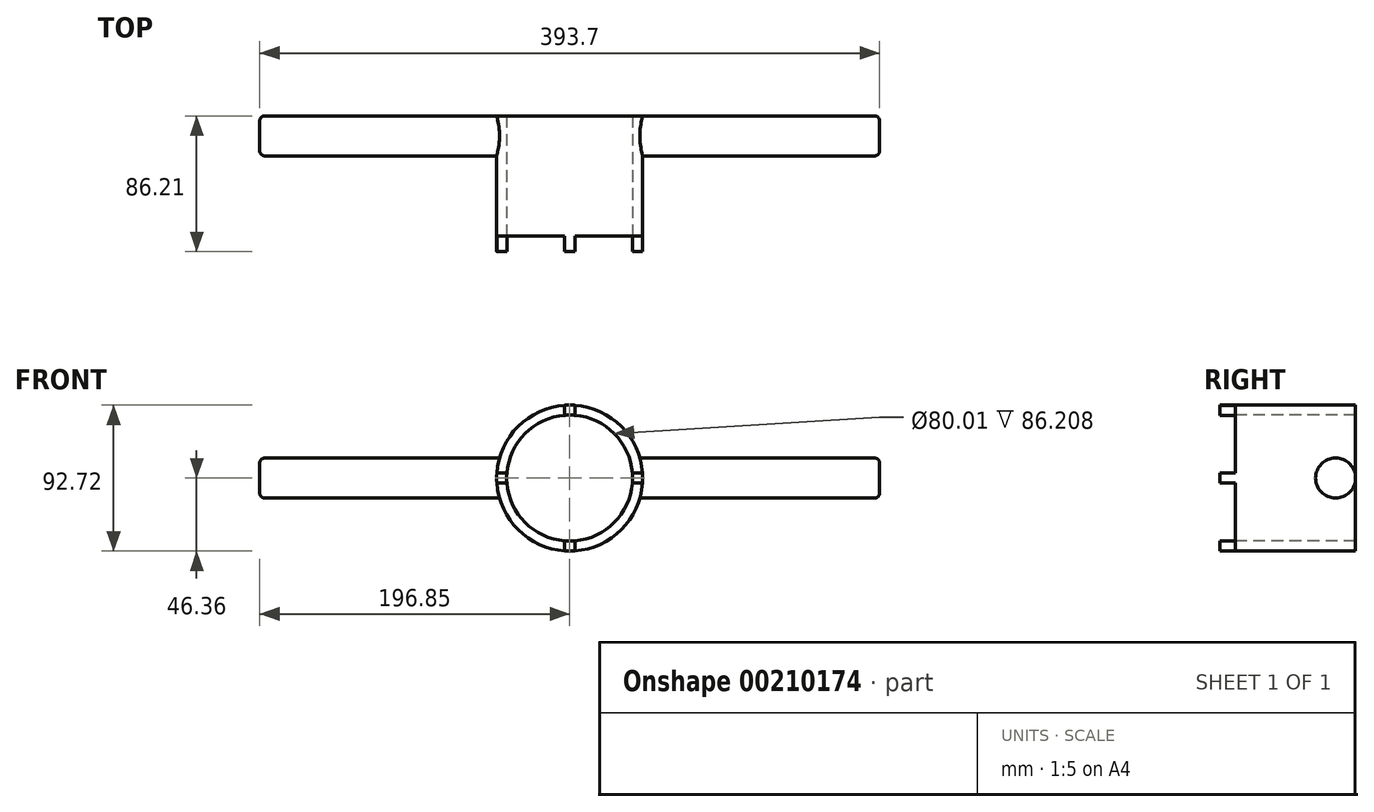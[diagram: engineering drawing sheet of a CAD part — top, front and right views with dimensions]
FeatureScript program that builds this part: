
annotation { "Feature Type Name" : "Feature", "Feature Type Description" : "" }
export const myFeature = defineFeature(function(context is Context, id is Id, definition is map)
    precondition{}
    {
        {
            var Q0;
            Q0=qCreatedBy(makeId("Front.planeOp"),FACE);
            var sketch = newSketch(context, id + "F0", { "sketchPlane" : qUnion([Q0])});
            skCircle(sketch, "E0", {"center": v(0, 0) * mm, "radius": 40 * mm});
            skCircle(sketch, "E1", {"center": v(0, 0) * mm, "radius": 46.35 * mm});
            skSolve(sketch);
        }
        {
            var Q0;
            Q0=makeQuery(id+"F0.imprint","IMPRINT",FACE,{"disambiguationData":[TD([[makeQuery(id+"F0.imprint","IMPRINT",EDGE,{"derivedFrom":sQuery(id+"F0.wireOp",EDGE,"E0")}),-1.0]])]});
            extrude(context, id + "F1", {"entities" : qUnion([Q0]), "oppositeDirection" : true, "depth" : 76.2 * mm});
        }
        {
            var Q0;
            Q0=makeQuery(id+"F1.opExtrude","CAP_FACE",FACE,{"disambiguationData":[OSD([sQuery(id+"F0.wireOp",EDGE,"E0"),sQuery(id+"F0.wireOp",EDGE,"E1")])],"isStart":true});
            var sketch = newSketch(context, id + "F2", { "sketchPlane" : qUnion([Q0])});
            skLineSegment(sketch, "E2.bottom", {"start": v(0, 48.23) * mm, "end": v(3.25, 48.23) * mm});
            skLineSegment(sketch, "E2.top", {"start": v(0, -47.48) * mm, "end": v(3.25, -47.48) * mm});
            skLineSegment(sketch, "E2.left", {"start": v(0, 48.23) * mm, "end": v(0, -47.48) * mm});
            skLineSegment(sketch, "E2.right", {"start": v(3.25, 48.23) * mm, "end": v(3.25, -47.48) * mm});
            skLineSegment(sketch, "E3.MirrorCS", {"start": v(0, 48.23) * mm, "end": v(-3.25, 48.23) * mm});
            skLineSegment(sketch, "E4.MirrorCS", {"start": v(-3.25, 48.23) * mm, "end": v(-3.25, -47.48) * mm});
            skLineSegment(sketch, "E5.MirrorCS", {"start": v(0, -47.48) * mm, "end": v(-3.25, -47.48) * mm});
            skSolve(sketch);
        }
        {
            var Q0;
            {var subQ0=sQuery(id+"F2.wireOp",EDGE,"E4.MirrorCS");var subQ1=makeQuery(id+"F1.opExtrude","CAP_EDGE",EDGE,{"disambiguationData":[OSD([sQuery(id+"F0.wireOp",EDGE,"E1")])],"isStart":true});var subQ2=makeQuery(id+"F2.imprint","INTERSECT",VERTEX,{"disambiguationData":[OD(0.0)],"derivedFrom":[subQ1,subQ0]});Q0=makeQuery(id+"F2.imprint","IMPRINT",FACE,{"disambiguationData":[TD([[makeQuery(id+"F2.imprint","IMPRINT",EDGE,{"disambiguationData":[TD([[subQ2,-1.0]])],"derivedFrom":subQ0}),-1.0]])]});}
            var sketch = newSketch(context, id + "F3", { "sketchPlane" : qUnion([Q0])});
            skLineSegment(sketch, "E6.bottom", {"start": v(0, 0) * mm, "end": v(50.37, 0) * mm});
            skLineSegment(sketch, "E6.top", {"start": v(0, 3.25) * mm, "end": v(50.37, 3.25) * mm});
            skLineSegment(sketch, "E6.left", {"start": v(0, 0) * mm, "end": v(0, 3.25) * mm});
            skLineSegment(sketch, "E6.right", {"start": v(50.37, 0) * mm, "end": v(50.37, 3.25) * mm});
            skLineSegment(sketch, "E7.MirrorCS", {"start": v(0, -3.25) * mm, "end": v(50.37, -3.25) * mm});
            skLineSegment(sketch, "E8.MirrorCS", {"start": v(50.37, 0) * mm, "end": v(50.37, -3.25) * mm});
            skLineSegment(sketch, "E9.MirrorCS", {"start": v(0, -3.25) * mm, "end": v(-50.37, -3.25) * mm});
            skLineSegment(sketch, "E10.MirrorCS", {"start": v(0, 3.25) * mm, "end": v(-50.37, 3.25) * mm});
            skLineSegment(sketch, "E11.MirrorCS", {"start": v(-50.37, 0) * mm, "end": v(-50.37, -3.25) * mm});
            skLineSegment(sketch, "E12.MirrorCS", {"start": v(-50.37, 0) * mm, "end": v(-50.37, 3.25) * mm});
            skSolve(sketch);
        }
        {
            var Q0;
            {var subQ0=sQuery(id+"F2.wireOp",EDGE,"E2.left");var subQ1=makeQuery(id+"F1.opExtrude","CAP_EDGE",EDGE,{"disambiguationData":[OSD([sQuery(id+"F0.wireOp",EDGE,"E1")])],"isStart":true});var subQ2=makeQuery(id+"F2.imprint","INTERSECT",VERTEX,{"disambiguationData":[OD(0.0)],"derivedFrom":[subQ1,subQ0]});Q0=makeQuery(id+"F2.imprint","IMPRINT",FACE,{"disambiguationData":[TD([[makeQuery(id+"F2.imprint","IMPRINT",EDGE,{"disambiguationData":[TD([[subQ2,-1.0]])],"derivedFrom":subQ0}),-1.0]])]});}
            var Q1;
            {var subQ0=sQuery(id+"F2.wireOp",EDGE,"E2.left");var subQ1=makeQuery(id+"F1.opExtrude","CAP_EDGE",EDGE,{"disambiguationData":[OSD([sQuery(id+"F0.wireOp",EDGE,"E1")])],"isStart":true});var subQ2=makeQuery(id+"F2.imprint","INTERSECT",VERTEX,{"disambiguationData":[OD(0.0)],"derivedFrom":[subQ1,subQ0]});Q1=makeQuery(id+"F2.imprint","IMPRINT",FACE,{"disambiguationData":[TD([[makeQuery(id+"F2.imprint","IMPRINT",EDGE,{"disambiguationData":[TD([[subQ2,-1.0]])],"derivedFrom":subQ0}),1.0]])]});}
            var Q2;
            {var subQ0=sQuery(id+"F2.wireOp",EDGE,"E2.left");var subQ1=makeQuery(id+"F1.opExtrude","CAP_EDGE",EDGE,{"disambiguationData":[OSD([sQuery(id+"F0.wireOp",EDGE,"E0")])],"isStart":true});var subQ2=makeQuery(id+"F2.imprint","INTERSECT",VERTEX,{"disambiguationData":[OD(1.0)],"derivedFrom":[subQ1,subQ0]});Q2=makeQuery(id+"F2.imprint","IMPRINT",FACE,{"disambiguationData":[TD([[makeQuery(id+"F2.imprint","IMPRINT",EDGE,{"disambiguationData":[TD([[subQ2,-1.0]])],"derivedFrom":subQ0}),1.0]])]});}
            var Q3;
            {var subQ0=sQuery(id+"F2.wireOp",EDGE,"E2.left");var subQ1=makeQuery(id+"F1.opExtrude","CAP_EDGE",EDGE,{"disambiguationData":[OSD([sQuery(id+"F0.wireOp",EDGE,"E0")])],"isStart":true});var subQ2=makeQuery(id+"F2.imprint","INTERSECT",VERTEX,{"disambiguationData":[OD(1.0)],"derivedFrom":[subQ1,subQ0]});Q3=makeQuery(id+"F2.imprint","IMPRINT",FACE,{"disambiguationData":[TD([[makeQuery(id+"F2.imprint","IMPRINT",EDGE,{"disambiguationData":[TD([[subQ2,-1.0]])],"derivedFrom":subQ0}),-1.0]])]});}
            var Q4;
            {var subQ0=sQuery(id+"F3.wireOp",EDGE,"E9.MirrorCS");var subQ1=sQuery(id+"F2.wireOp",EDGE,"E4.MirrorCS");var subQ2=makeQuery(id+"F1.opExtrude","CAP_EDGE",EDGE,{"disambiguationData":[OSD([sQuery(id+"F0.wireOp",EDGE,"E0")])],"isStart":true});var subQ3=makeQuery(id+"F2.imprint","IMPRINT",EDGE,{"disambiguationData":[TD([[makeQuery(id+"F2.imprint","INTERSECT",VERTEX,{"disambiguationData":[OD(0.0)],"derivedFrom":[subQ2,subQ1]}),-1.0]])],"derivedFrom":subQ2});var subQ4=makeQuery(id+"F3.imprint","INTERSECT",VERTEX,{"derivedFrom":[subQ3,subQ0]});Q4=makeQuery(id+"F3.imprint","IMPRINT",FACE,{"disambiguationData":[TD([[makeQuery(id+"F3.imprint","IMPRINT",EDGE,{"disambiguationData":[TD([[subQ4,-1.0]])],"derivedFrom":subQ0}),-1.0]])]});}
            extrude(context, id + "F4", {"entities" : qUnion([Q0, Q1, Q2, Q3, Q4]), "operationType" : NewBodyOperationType.ADD, "depth" : 10 * mm});
        }
        {
            var Q0;
            {var subQ0=sQuery(id+"F2.wireOp",EDGE,"E2.right");var subQ1=sQuery(id+"F0.wireOp",EDGE,"E1");var subQ2=makeQuery(id+"F1.opExtrude","CAP_EDGE",EDGE,{"disambiguationData":[OSD([subQ1])],"isStart":true});var subQ4=sQuery(id+"F0.wireOp",EDGE,"E0");var subQ16=makeQuery(id+"F2.imprint","INTERSECT",VERTEX,{"disambiguationData":[OD(0.0)],"derivedFrom":[subQ2,subQ0]});Q0=makeQuery(id+"F4.boolean.opBoolean","SPLIT",FACE,{"disambiguationData":[TD([makeQuery(id+"F4.opExtrude","SWEPT_FACE",FACE,{"disambiguationData":[OSD([subQ0]),TDD([makeQuery(id+"F2.imprint","IMPRINT",EDGE,{"disambiguationData":[TD([[subQ16,-1.0]])],"derivedFrom":subQ0})])]})])],"derivedFrom":makeQuery(id+"F1.opExtrude","CAP_FACE",FACE,{"disambiguationData":[OSD([subQ4,subQ1])],"isStart":true})});}
            var sketch = newSketch(context, id + "F5", { "sketchPlane" : qUnion([Q0])});
            skLineSegment(sketch, "E13.bottom", {"start": v(0, 0) * mm, "end": v(46.56, 0) * mm});
            skLineSegment(sketch, "E13.top", {"start": v(0, 3.25) * mm, "end": v(46.56, 3.25) * mm});
            skLineSegment(sketch, "E13.left", {"start": v(0, 0) * mm, "end": v(0, 3.25) * mm});
            skLineSegment(sketch, "E13.right", {"start": v(46.56, 0) * mm, "end": v(46.56, 3.25) * mm});
            skLineSegment(sketch, "E14.MirrorCS", {"start": v(0, -3.25) * mm, "end": v(46.56, -3.25) * mm});
            skLineSegment(sketch, "E15.MirrorCS", {"start": v(46.56, 0) * mm, "end": v(46.56, -3.25) * mm});
            skSolve(sketch);
        }
        {
            var Q0;
            {var subQ0=sQuery(id+"F5.wireOp",EDGE,"E13.bottom");var subQ1=sQuery(id+"F2.wireOp",EDGE,"E2.right");var subQ2=sQuery(id+"F0.wireOp",EDGE,"E1");var subQ3=makeQuery(id+"F1.opExtrude","CAP_EDGE",EDGE,{"disambiguationData":[OSD([subQ2])],"isStart":true});var subQ13=makeQuery(id+"F2.imprint","INTERSECT",VERTEX,{"disambiguationData":[OD(0.0)],"derivedFrom":[subQ3,subQ1]});var subQ15=makeQuery(id+"F4.opExtrude","SWEPT_FACE",FACE,{"disambiguationData":[OSD([subQ1]),TDD([makeQuery(id+"F2.imprint","IMPRINT",EDGE,{"disambiguationData":[TD([[subQ13,-1.0]])],"derivedFrom":subQ1})])]});var subQ29=makeQuery(id+"F4.boolean.opBoolean","SPLIT",EDGE,{"disambiguationData":[TD([subQ15])],"derivedFrom":subQ3});var subQ30=makeQuery(id+"F5.imprint","INTERSECT",VERTEX,{"derivedFrom":[subQ29,subQ0]});Q0=makeQuery(id+"F5.imprint","IMPRINT",FACE,{"disambiguationData":[TD([[makeQuery(id+"F5.imprint","IMPRINT",EDGE,{"disambiguationData":[TD([[subQ30,1.0]])],"derivedFrom":subQ0}),1.0]])]});}
            var Q1;
            {var subQ0=sQuery(id+"F5.wireOp",EDGE,"E13.bottom");var subQ1=sQuery(id+"F2.wireOp",EDGE,"E2.right");var subQ2=sQuery(id+"F0.wireOp",EDGE,"E1");var subQ3=makeQuery(id+"F1.opExtrude","CAP_EDGE",EDGE,{"disambiguationData":[OSD([subQ2])],"isStart":true});var subQ13=makeQuery(id+"F2.imprint","INTERSECT",VERTEX,{"disambiguationData":[OD(0.0)],"derivedFrom":[subQ3,subQ1]});var subQ15=makeQuery(id+"F4.opExtrude","SWEPT_FACE",FACE,{"disambiguationData":[OSD([subQ1]),TDD([makeQuery(id+"F2.imprint","IMPRINT",EDGE,{"disambiguationData":[TD([[subQ13,-1.0]])],"derivedFrom":subQ1})])]});var subQ29=makeQuery(id+"F4.boolean.opBoolean","SPLIT",EDGE,{"disambiguationData":[TD([subQ15])],"derivedFrom":subQ3});var subQ30=makeQuery(id+"F5.imprint","INTERSECT",VERTEX,{"derivedFrom":[subQ29,subQ0]});Q1=makeQuery(id+"F5.imprint","IMPRINT",FACE,{"disambiguationData":[TD([[makeQuery(id+"F5.imprint","IMPRINT",EDGE,{"disambiguationData":[TD([[subQ30,1.0]])],"derivedFrom":subQ0}),-1.0]])]});}
            extrude(context, id + "F6", {"entities" : qUnion([Q0, Q1]), "operationType" : NewBodyOperationType.ADD, "depth" : 10 * mm});
        }
        {
            var Q0;
            Q0=qCreatedBy(makeId("Right.planeOp"),FACE);
            var sketch = newSketch(context, id + "F7", { "sketchPlane" : qUnion([Q0])});
            skCircle(sketch, "E16", {"center": v(63.5, 0) * mm, "radius": 12.7 * mm});
            skSolve(sketch);
        }
        {
            var Q0;
            Q0=makeQuery(id+"F7.imprint","IMPRINT",FACE,{"disambiguationData":[TD([[makeQuery(id+"F7.imprint","IMPRINT",EDGE,{"derivedFrom":sQuery(id+"F7.wireOp",EDGE,"E16")}),1.0]])]});
            cPlane(context, id + "F8", {"entities" : qUnion([Q0]), "cplaneType" : CPlaneType.OFFSET, "offset" : 40 * mm, "width" : 152.4 * mm, "height" : 152.4 * mm});
        }
        {
            var Q0;
            Q0=qCreatedBy(id+"F8.planeOp",FACE);
            var sketch = newSketch(context, id + "F9", { "sketchPlane" : qUnion([Q0])});
            skCircle(sketch, "E17", {"center": v(63.5, 0) * mm, "radius": 12.7 * mm});
            skSolve(sketch);
        }
        {
            var Q0;
            Q0 = qSketchRegion(id + "F9", true);
            extrude(context, id + "F10", {"entities" : qUnion([Q0]), "operationType" : NewBodyOperationType.ADD, "depth" : 156.84 * mm});
        }
        {
            var Q0;
            Q0=makeQuery(id+"F10.opExtrude","CAP_EDGE",EDGE,{"disambiguationData":[OSD([sQuery(id+"F9.wireOp",EDGE,"E17")])],"isStart":false});
            fillet(context, id + "F11", {"entities" : qUnion([Q0]), "radius" : 3.17 * mm, "tangentPropagation" : true, "allowEdgeOverflow" : false});
        }
        {
            var Q0;
            Q0=makeQuery(id+"F1.opExtrude","SWEPT_BODY",BODY,{"disambiguationData":[OSD([sQuery(id+"F0.wireOp",EDGE,"E0"),sQuery(id+"F0.wireOp",EDGE,"E1")])]});
            var Q1;
            Q1=qCreatedBy(makeId("Right.planeOp"),FACE);
            mirror(context, id + "F12", {"operationType" : NewBodyOperationType.ADD, "entities" : qUnion([Q0]), "mirrorPlane" : qUnion([Q1])});
        }
    });
